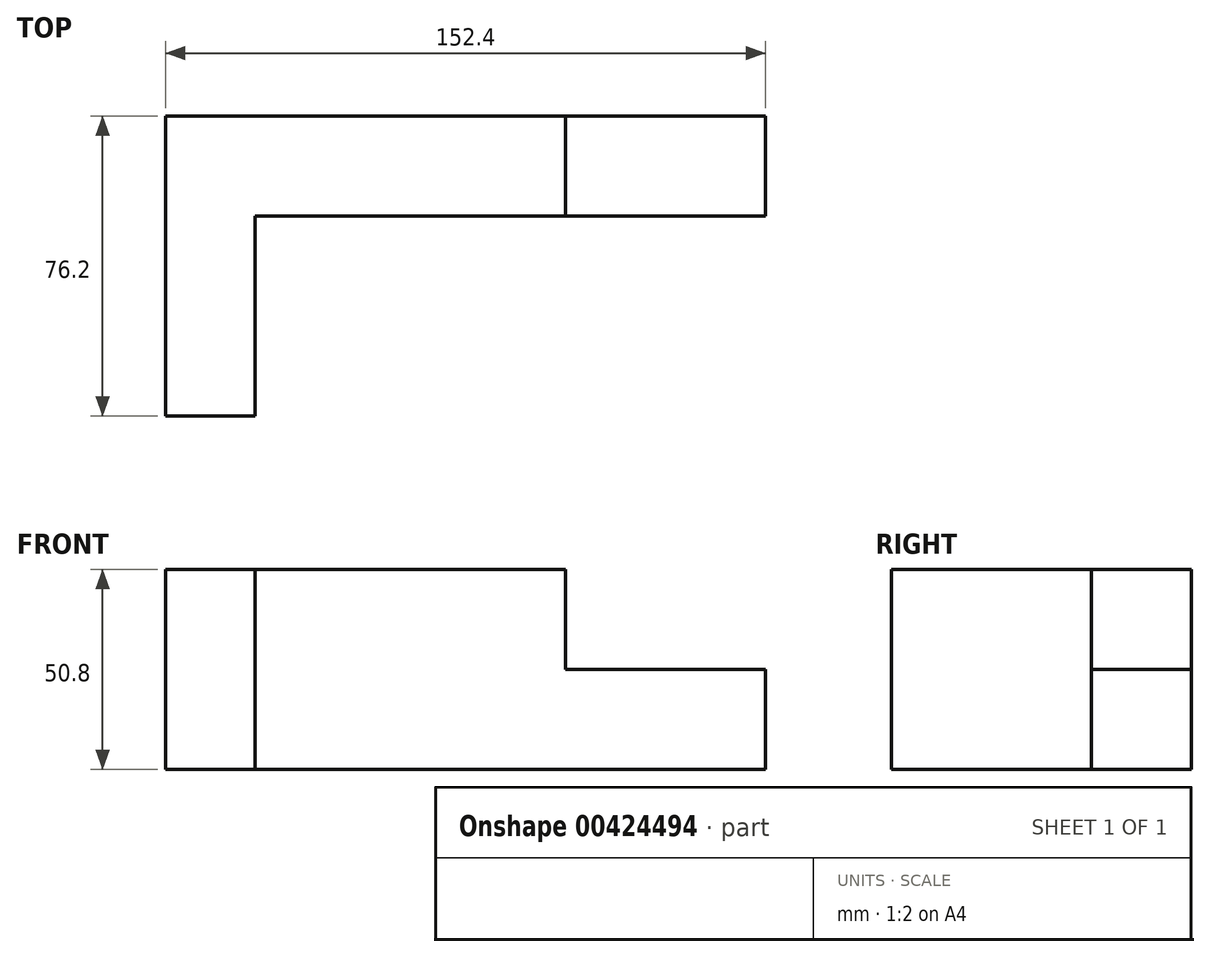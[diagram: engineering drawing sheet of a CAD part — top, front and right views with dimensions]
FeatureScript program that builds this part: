
annotation { "Feature Type Name" : "Feature", "Feature Type Description" : "" }
export const myFeature = defineFeature(function(context is Context, id is Id, definition is map)
    precondition{}
    {
        {
            var Q0;
            Q0=qCreatedBy(makeId("Front.planeOp"),FACE);
            var sketch = newSketch(context, id + "F0", { "sketchPlane" : qUnion([Q0])});
            skLineSegment(sketch, "E0", {"start": v(0, 0) * mm, "end": v(0, 50.8) * mm});
            skLineSegment(sketch, "E1", {"start": v(0, 50.8) * mm, "end": v(152.4, 50.8) * mm});
            skLineSegment(sketch, "E2", {"start": v(152.4, 50.8) * mm, "end": v(152.4, 0) * mm});
            skLineSegment(sketch, "E3", {"start": v(152.4, 0) * mm, "end": v(0, 0) * mm});
            skSolve(sketch);
        }
        {
            var Q0;
            Q0=makeQuery(id+"F0.imprint","IMPRINT",FACE,{"disambiguationData":[TD([[makeQuery(id+"F0.imprint","IMPRINT",EDGE,{"derivedFrom":sQuery(id+"F0.wireOp",EDGE,"E0")}),-1.0]])]});
            extrude(context, id + "F1", {"entities" : qUnion([Q0]), "depth" : 76.2 * mm});
        }
        {
            var Q0;
            Q0=makeQuery(id+"F1.opExtrude","SWEPT_FACE",FACE,{"disambiguationData":[OSD([sQuery(id+"F0.wireOp",EDGE,"E1")])]});
            var sketch = newSketch(context, id + "F2", { "sketchPlane" : qUnion([Q0])});
            skLineSegment(sketch, "E4", {"start": v(22.76, -76.2) * mm, "end": v(22.76, -25.4) * mm});
            skLineSegment(sketch, "E5", {"start": v(22.76, -25.4) * mm, "end": v(152.4, -25.4) * mm});
            skLineSegment(sketch, "E6", {"start": v(152.4, -25.4) * mm, "end": v(152.4, -76.2) * mm});
            skLineSegment(sketch, "E7", {"start": v(152.4, -76.2) * mm, "end": v(22.76, -76.2) * mm});
            skSolve(sketch);
        }
        {
            var Q0;
            Q0=makeQuery(id+"F2.imprint","IMPRINT",FACE,{"disambiguationData":[TD([[makeQuery(id+"F2.imprint","IMPRINT",EDGE,{"derivedFrom":sQuery(id+"F2.wireOp",EDGE,"E4")}),-1.0]])]});
            extrude(context, id + "F3", {"entities" : qUnion([Q0]), "operationType" : NewBodyOperationType.REMOVE, "oppositeDirection" : true, "depth" : 50.8 * mm});
        }
        {
            var Q0;
            Q0=makeQuery(id+"F3.boolean.opBoolean","COPY",FACE,{"derivedFrom":makeQuery(id+"F3.opExtrude","SWEPT_FACE",FACE,{"disambiguationData":[OSD([sQuery(id+"F2.wireOp",EDGE,"E5")])]})});
            var sketch = newSketch(context, id + "F4", { "sketchPlane" : qUnion([Q0])});
            skLineSegment(sketch, "E8", {"start": v(152.4, 25.4) * mm, "end": v(101.6, 25.4) * mm});
            skLineSegment(sketch, "E9", {"start": v(101.6, 25.4) * mm, "end": v(101.6, 50.8) * mm});
            skLineSegment(sketch, "E10", {"start": v(101.6, 50.8) * mm, "end": v(152.4, 50.8) * mm});
            skLineSegment(sketch, "E11", {"start": v(152.4, 50.8) * mm, "end": v(152.4, 25.4) * mm});
            skSolve(sketch);
        }
        {
            var Q0;
            Q0=makeQuery(id+"F4.imprint","IMPRINT",FACE,{"disambiguationData":[TD([[makeQuery(id+"F4.imprint","IMPRINT",EDGE,{"derivedFrom":sQuery(id+"F4.wireOp",EDGE,"E8")}),-1.0]])]});
            extrude(context, id + "F5", {"entities" : qUnion([Q0]), "operationType" : NewBodyOperationType.REMOVE, "oppositeDirection" : true, "depth" : 25.4 * mm});
        }
    });
